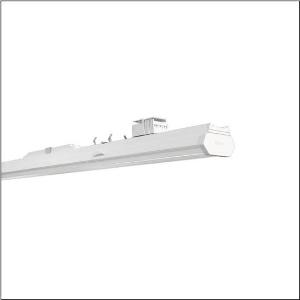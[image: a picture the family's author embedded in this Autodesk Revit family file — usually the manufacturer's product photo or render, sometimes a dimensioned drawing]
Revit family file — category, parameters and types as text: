
# Revit family: licross_r__11_protected_extreme_mo_51tp12dn495ge_fe34
name_source: partatom
category: Lighting Fixtures
units: mm (PartAtom-declared; Revit-internal decimal feet)

## family parameters
Cut with Voids When Loaded = No
Host = Face
Light Source = No
Part Type = Normal
Room Calculation Point = No
Round Connector Dimension = Use Diameter
Shared = No

## types (1)
- --- (1 x LED, 9980 lm, 57.1 W, 4000K)
    Apparent Load = 57 VA
    CIE Flux Codes = 73 92 98 99 100
    Color Rendering = 80
    Color Temperature = 4000K
    Default Elevation = 1800 mm
    Description = Licross® 11 Protected extreme MO, luminaire insert, of sheet steel, galvanised, coil coated, white, length: 1.500mm, width: 90mm, height: 101mm, LED rated luminous flux: 9.980lm, light colour: 840, control gear: DALI 2, with plug, 5-pole, with phase selection, mains connection: 220..240V, AC, 50/60Hz, rated input power: 57W, halogen-free wiring, primary optical cover: cover, of PMMA, light emission: direct distribution, primary light characteristic: symmetric, protection rating (complete): IP64, insulation class (complete): insulation class I (protective earthing), certification: CE, ENEC, VDE, UKCA, protection symbol: D if used in an environment with conductive dust loads with corresponding accessories, impact resistance: IK06, permissible ambient temperature for indoor applications: -40..+35°C, corresponds to IFS (International Featured Standards) requirements for safety and quality in the food industry, reducing of maximum allowable ambient temperature of 5°C with ceiling mounting, LABS conformity tested according to VDMA 24364:2018-05, packaging unit: 1 piece
    Height = 92 mm
    Lamp = 1 x LED
    Lamp Light Flux = 9980 lm
    Lamp Power = 57.1 W
    Lamp count = 1
    Length = 1500 mm
    Luminous efficacy = 175 lm/W
    Manufacturer = Siteco
    ModVariant = No
    Model = 51TP12DN495GE
    Mounting Place = Ceiling
    Mounting Type = Pendant
    Number of Poles = 1
    OnlyDefault = Yes
    Power Factor = 1
    Product Name = Licross® 11 Protected extreme MO
    Product group = luminaire insert
    ProductGroupID = 901
    Protection Class = Protection class I
    Protection Degree = IP 64
    RLX_Detail_Level = 1
    RLX_Emergency_Light_Flux = 0 lm
    RLX_Emergency_Type = 0
    RLX_Emergency_Type_DB = No
    RlxData = <blob elided: 24385 chars, md5=eb00d19b>
    Socket = socket
    Standby Power = 0 W
    System Light Flux = 9980 lm
    System Power = 57 W
    Type Comments = factory setting: luminous flux: 100 % | dim-lin: 254 | 378 mA
    Type Image = l_1256148.jpg
    URL = http://relux.com
    VarID = @adj_034967
    Voltage = 0 V
    Weight = 0.00 kg
    Width = 88 mm

## geometry (parser evidence)
native form markers: Blend x4, Sweep x11
no freeform markers — native parametric forms only
